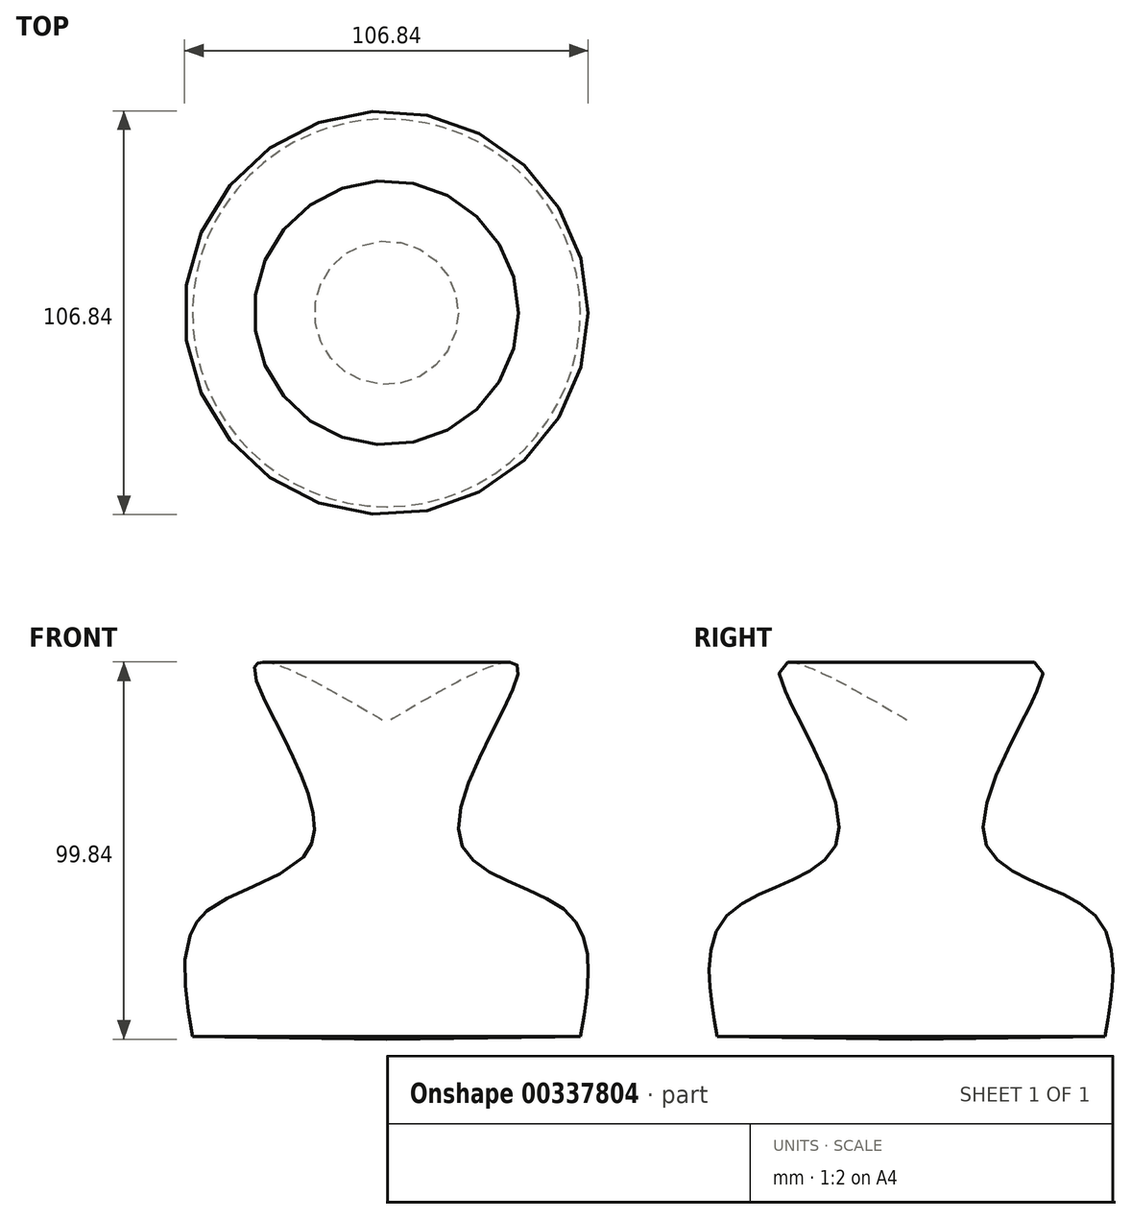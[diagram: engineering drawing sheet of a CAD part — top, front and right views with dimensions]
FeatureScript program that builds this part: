
annotation { "Feature Type Name" : "Feature", "Feature Type Description" : "" }
export const myFeature = defineFeature(function(context is Context, id is Id, definition is map)
    precondition{}
    {
        {
            var Q0;
            Q0=qCreatedBy(makeId("Front.planeOp"),FACE);
            var sketch = newSketch(context, id + "F0", { "sketchPlane" : qUnion([Q0])});
            skFitSpline(sketch, "E0", {"points": [v(122.13, -2.2) * mm, v(90.38, 90.76) * mm], "startDerivative": vector(-31.75, 92.96) * mm, "endDerivative": vector(-31.75, 92.96) * mm});
            skFitSpline(sketch, "E1", {"points": [v(51.33, 0.74) * mm, v(48.05, 33.45) * mm, v(19.26, 53.5) * mm, v(34.92, 98.24) * mm, v(0, 83.9) * mm], "startDerivative": vector(28.57, 164.66) * mm, "endDerivative": vector(-205.2, -119.88) * mm});
            skLineSegment(sketch, "E2", {"start": v(0, 83.9) * mm, "end": v(0, 0) * mm});
            skLineSegment(sketch, "E3", {"start": v(0, 0) * mm, "end": v(51.33, 0.74) * mm});
            skSolve(sketch);
        }
        {
            var Q0;
            Q0 = qSketchRegion(id + "F0", true);
            var Q1;
            Q1=sQuery(id+"F0.wireOp",EDGE,"E2");
            revolve(context, id + "F1", {"entities" : qUnion([Q0]), "axis" : qUnion([Q1]), "revolveType" : RevolveType.FULL});
        }
    });
